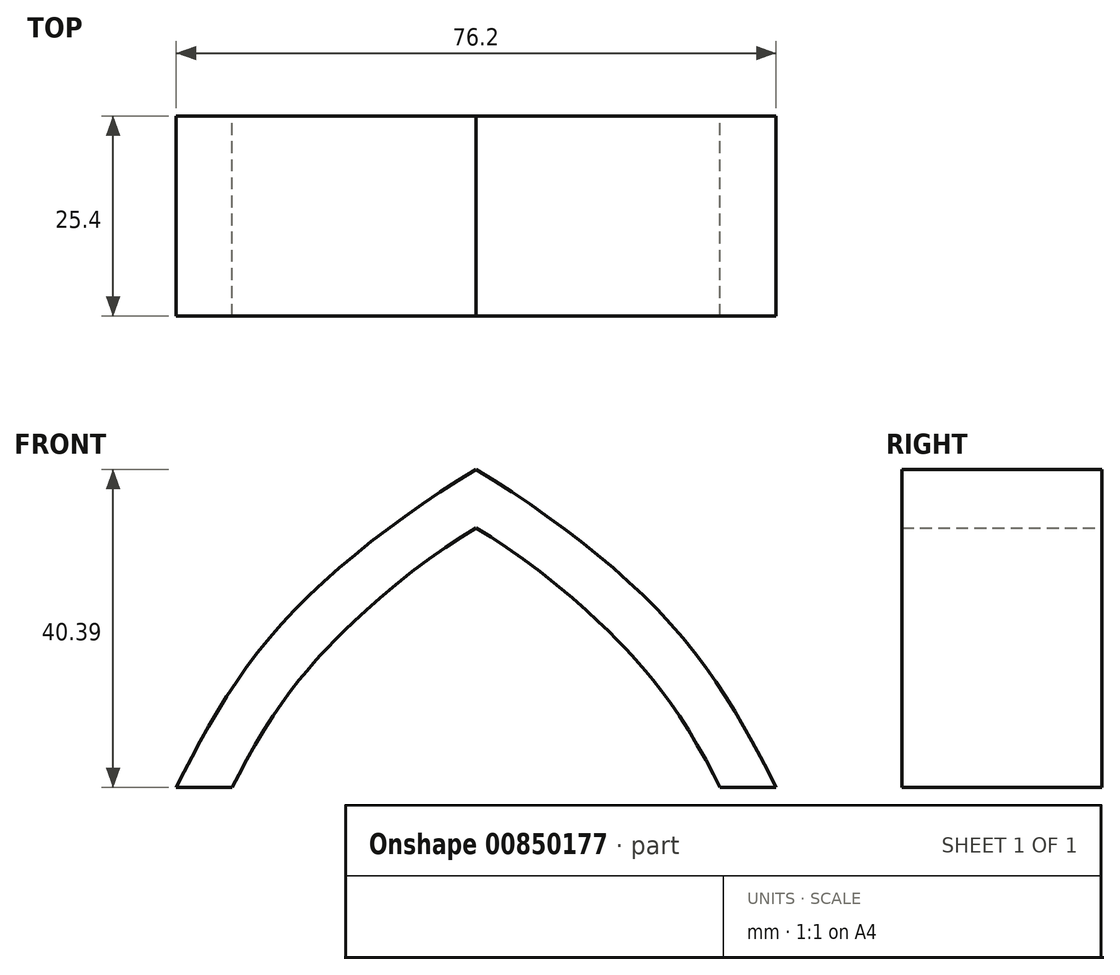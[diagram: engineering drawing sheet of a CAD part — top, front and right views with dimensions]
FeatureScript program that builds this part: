
annotation { "Feature Type Name" : "Feature", "Feature Type Description" : "" }
export const myFeature = defineFeature(function(context is Context, id is Id, definition is map)
    precondition{}
    {
        {
            var Q0;
            Q0=qCreatedBy(makeId("Front.planeOp"),FACE);
            var sketch = newSketch(context, id + "F0", { "sketchPlane" : qUnion([Q0])});
            skLineSegment(sketch, "E0", {"start": v(-30.97, 0) * mm, "end": v(-38.1, 0) * mm});
            skLineSegment(sketch, "E1", {"start": v(30.97, 0) * mm, "end": v(38.1, 0) * mm});
            skFitSpline(sketch, "E2", {"points": [v(-38.1, 0) * mm, v(-25.31, 20.1) * mm, v(0, 40.39) * mm], "startDerivative": vector(22.77, 45.17) * mm, "endDerivative": vector(52.75, 31.96) * mm});
            skFitSpline(sketch, "E3.MirrorCS", {"points": [v(38.1, 0) * mm, v(25.31, 20.1) * mm, v(0, 40.39) * mm], "startDerivative": vector(-22.77, 45.17) * mm, "endDerivative": vector(-52.75, 31.96) * mm});
            skFitSpline(sketch, "E4.0", {"points": [v(-32.43, -2.86) * mm, v(-31.5, -1) * mm, v(-29.64, 2.6) * mm, v(-26.67, 7.75) * mm, v(-23.88, 11.83) * mm, v(-21.66, 14.62) * mm, v(-20.3, 16.18) * mm, v(-18.88, 17.75) * mm, v(-16.95, 19.72) * mm, v(-13.6, 22.83) * mm, v(-7.16, 28.18) * mm, v(-0.92, 32.4) * mm, v(3.3, 34.96) * mm]});
            skFitSpline(sketch, "E5.0", {"points": [v(32.43, -2.86) * mm, v(31.5, -1) * mm, v(29.64, 2.6) * mm, v(26.67, 7.75) * mm, v(23.88, 11.83) * mm, v(21.66, 14.62) * mm, v(20.3, 16.18) * mm, v(18.88, 17.75) * mm, v(16.95, 19.72) * mm, v(13.6, 22.83) * mm, v(7.16, 28.18) * mm, v(0.92, 32.4) * mm, v(-3.3, 34.96) * mm]});
            skPoint(sketch, "E6.orphan", {"position": v(0, 2.29) * mm});
            skSolve(sketch);
        }
        {
            var Q0;
            Q0=makeQuery(id+"F0.imprint","IMPRINT",FACE,{"disambiguationData":[TD([[makeQuery(id+"F0.imprint","IMPRINT",EDGE,{"derivedFrom":sQuery(id+"F0.wireOp",EDGE,"E0")}),-1.0]])]});
            extrude(context, id + "F1", {"entities" : qUnion([Q0]), "depth" : 25.4 * mm, "offsetDistance" : 25.4 * mm});
        }
    });
